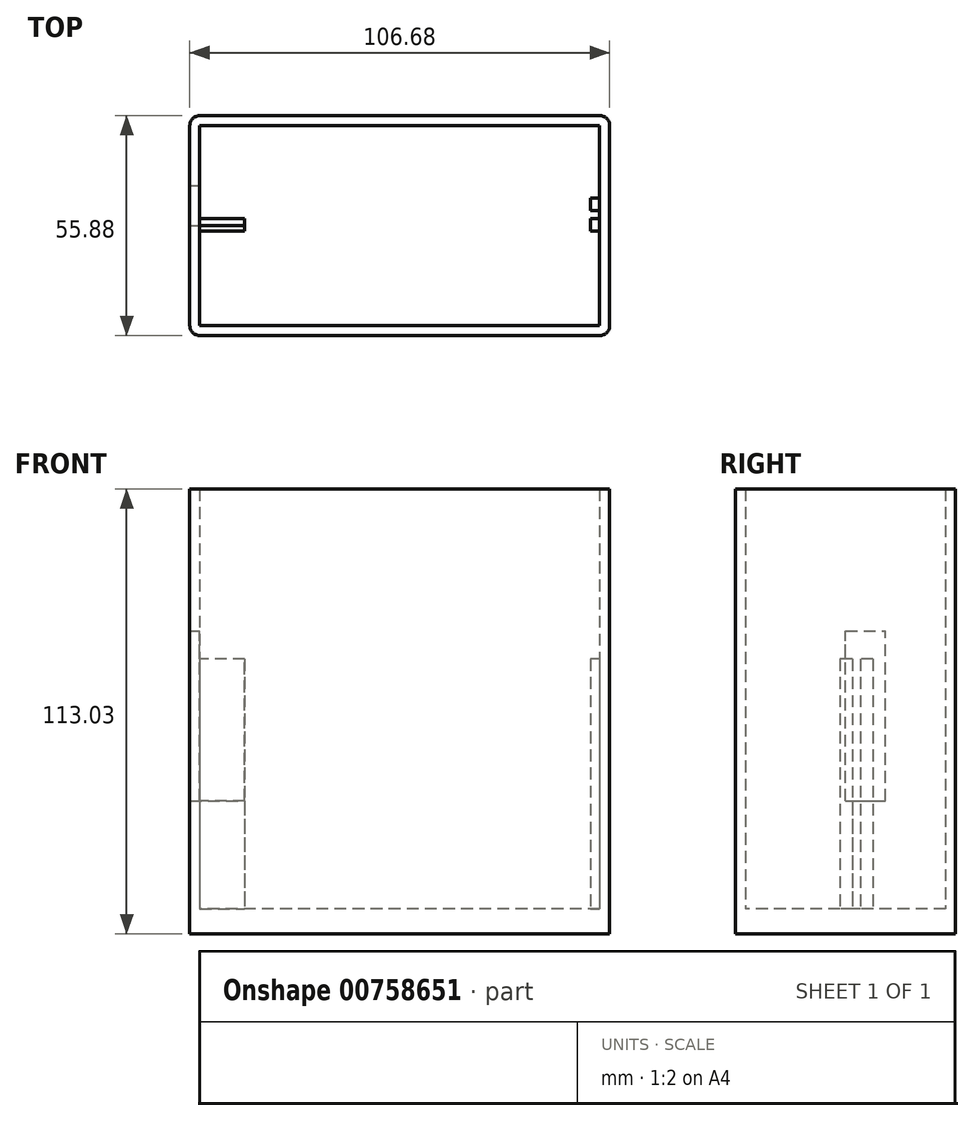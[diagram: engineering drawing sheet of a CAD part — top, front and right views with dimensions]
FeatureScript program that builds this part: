
annotation { "Feature Type Name" : "Feature", "Feature Type Description" : "" }
export const myFeature = defineFeature(function(context is Context, id is Id, definition is map)
    precondition{}
    {
        {
            var Q0;
            Q0=qCreatedBy(makeId("Top.planeOp"),FACE);
            var sketch = newSketch(context, id + "F0", { "sketchPlane" : qUnion([Q0])});
            skLineSegment(sketch, "E0.bottom", {"start": v(50.8, 25.4) * mm, "end": v(-50.8, 25.4) * mm});
            skLineSegment(sketch, "E0.top", {"start": v(50.8, -25.4) * mm, "end": v(-50.8, -25.4) * mm});
            skLineSegment(sketch, "E0.left", {"start": v(50.8, 25.4) * mm, "end": v(50.8, -25.4) * mm});
            skLineSegment(sketch, "E0.right", {"start": v(-50.8, 25.4) * mm, "end": v(-50.8, -25.4) * mm});
            skPoint(sketch, "E0.middle", {"position": v(0, 0) * mm});
            skLineSegment(sketch, "E1.bottom", {"start": v(50.8, 27.94) * mm, "end": v(-50.8, 27.94) * mm});
            skLineSegment(sketch, "E1.top", {"start": v(50.8, -27.94) * mm, "end": v(-50.8, -27.94) * mm});
            skLineSegment(sketch, "E1.left", {"start": v(53.34, 25.4) * mm, "end": v(53.34, -25.4) * mm});
            skLineSegment(sketch, "E1.right", {"start": v(-53.34, 25.4) * mm, "end": v(-53.34, -25.4) * mm});
            skPoint(sketch, "E2.visualSharp", {"position": v(53.34, 27.94) * mm});
            skArc(sketch, "E2.filletArc", {"start": v(53.34, 25.4) * mm, "mid": v(52.6, 27.2) * mm, "end": v(50.8, 27.94) * mm});
            skPoint(sketch, "E3.visualSharp", {"position": v(-53.34, 27.94) * mm});
            skArc(sketch, "E3.filletArc", {"start": v(-50.8, 27.94) * mm, "mid": v(-52.6, 27.2) * mm, "end": v(-53.34, 25.4) * mm});
            skPoint(sketch, "E4.visualSharp", {"position": v(-53.34, -27.94) * mm});
            skArc(sketch, "E4.filletArc", {"start": v(-53.34, -25.4) * mm, "mid": v(-52.6, -27.2) * mm, "end": v(-50.8, -27.94) * mm});
            skPoint(sketch, "E5.visualSharp", {"position": v(53.34, -27.94) * mm});
            skArc(sketch, "E5.filletArc", {"start": v(50.8, -27.94) * mm, "mid": v(52.6, -27.2) * mm, "end": v(53.34, -25.4) * mm});
            skSolve(sketch);
        }
        {
            var Q0;
            Q0=makeQuery(id+"F0.imprint","IMPRINT",FACE,{"disambiguationData":[TD([[makeQuery(id+"F0.imprint","IMPRINT",EDGE,{"derivedFrom":sQuery(id+"F0.wireOp",EDGE,"E0.bottom")}),-1.0]])]});
            extrude(context, id + "F1", {"entities" : qUnion([Q0]), "depth" : 113.03 * mm, "offsetDistance" : 25.4 * mm});
        }
        {
            var Q0;
            Q0=qSketchRegion(id+"F0",true);
            var Q1;
            Q1=makeQuery(id+"F0.imprint","IMPRINT",FACE,{"disambiguationData":[TD([[makeQuery(id+"F0.imprint","IMPRINT",EDGE,{"derivedFrom":sQuery(id+"F0.wireOp",EDGE,"E0.bottom")}),1.0]])]});
            extrude(context, id + "F2", {"entities" : qUnion([Q0, Q1]), "operationType" : NewBodyOperationType.ADD, "depth" : 6.35 * mm, "offsetDistance" : 25.4 * mm});
        }
        {
            var Q0;
            Q0=makeQuery(id+"F2.opExtrude","CAP_FACE",FACE,{"disambiguationData":[OSD([sQuery(id+"F0.wireOp",EDGE,"E1.bottom"),sQuery(id+"F0.wireOp",EDGE,"E1.top"),sQuery(id+"F0.wireOp",EDGE,"E1.left"),sQuery(id+"F0.wireOp",EDGE,"E1.right"),sQuery(id+"F0.wireOp",EDGE,"BYKlQcYZ-631A-2yId-C92L-wMy8uTNsIFIs.bottom"),sQuery(id+"F0.wireOp",EDGE,"BYKlQcYZ-631A-2yId-C92L-wMy8uTNsIFIs.top"),sQuery(id+"F0.wireOp",EDGE,"BYKlQcYZ-631A-2yId-C92L-wMy8uTNsIFIs.left"),sQuery(id+"F0.wireOp",EDGE,"BYKlQcYZ-631A-2yId-C92L-wMy8uTNsIFIs.right"),sQuery(id+"F0.wireOp",EDGE,"E2.filletArc"),sQuery(id+"F0.wireOp",EDGE,"E3.filletArc"),sQuery(id+"F0.wireOp",EDGE,"E4.filletArc"),sQuery(id+"F0.wireOp",EDGE,"E5.filletArc")])],"isStart":false});
            var sketch = newSketch(context, id + "F3", { "sketchPlane" : qUnion([Q0])});
            skLineSegment(sketch, "E6", {"start": v(-50.8, 1.78) * mm, "end": v(-39.37, 1.78) * mm});
            skLineSegment(sketch, "E7", {"start": v(-39.37, 1.78) * mm, "end": v(-39.37, -1.4) * mm});
            skLineSegment(sketch, "E8", {"start": v(-39.37, -1.4) * mm, "end": v(-50.8, -1.4) * mm});
            skSolve(sketch);
        }
        {
            var Q0;
            Q0=qSketchRegion(id+"F3",true);
            var Q1;
            {var subQ0=sQuery(id+"F3.wireOp",EDGE,"lTtmv5Bm-ZFXb-4e8F-iXT5-zUQ0Jz6aJe3K");Q1=makeQuery(id+"F3.imprint","IMPRINT",FACE,{"disambiguationData":[TD([[makeQuery(id+"F3.imprint","IMPRINT",EDGE,{"derivedFrom":subQ0}),-1.0]])]});}
            var Q2;
            {var subQ0=sQuery(id+"F3.wireOp",EDGE,"E6");Q2=makeQuery(id+"F3.imprint","IMPRINT",FACE,{"disambiguationData":[TD([[makeQuery(id+"F3.imprint","IMPRINT",EDGE,{"derivedFrom":subQ0}),-1.0]])]});}
            extrude(context, id + "F4", {"entities" : qUnion([Q0, Q1, Q2]), "operationType" : NewBodyOperationType.ADD, "depth" : 63.5 * mm, "offsetDistance" : 25.4 * mm});
        }
        {
            var Q0;
            Q0=makeQuery(id+"F2.opExtrude","CAP_FACE",FACE,{"disambiguationData":[OSD([sQuery(id+"F0.wireOp",EDGE,"E1.bottom"),sQuery(id+"F0.wireOp",EDGE,"E1.top"),sQuery(id+"F0.wireOp",EDGE,"E1.left"),sQuery(id+"F0.wireOp",EDGE,"E1.right"),sQuery(id+"F0.wireOp",EDGE,"BYKlQcYZ-631A-2yId-C92L-wMy8uTNsIFIs.bottom"),sQuery(id+"F0.wireOp",EDGE,"BYKlQcYZ-631A-2yId-C92L-wMy8uTNsIFIs.top"),sQuery(id+"F0.wireOp",EDGE,"BYKlQcYZ-631A-2yId-C92L-wMy8uTNsIFIs.left"),sQuery(id+"F0.wireOp",EDGE,"BYKlQcYZ-631A-2yId-C92L-wMy8uTNsIFIs.right"),sQuery(id+"F0.wireOp",EDGE,"E2.filletArc"),sQuery(id+"F0.wireOp",EDGE,"E3.filletArc"),sQuery(id+"F0.wireOp",EDGE,"E4.filletArc"),sQuery(id+"F0.wireOp",EDGE,"E5.filletArc")])],"isStart":false});
            var sketch = newSketch(context, id + "F5", { "sketchPlane" : qUnion([Q0])});
            skLineSegment(sketch, "E9", {"start": v(50.8, 6.99) * mm, "end": v(48.51, 6.99) * mm});
            skLineSegment(sketch, "E10", {"start": v(48.51, 6.99) * mm, "end": v(48.51, 3.81) * mm});
            skLineSegment(sketch, "E11", {"start": v(48.51, 3.81) * mm, "end": v(50.8, 3.81) * mm});
            skLineSegment(sketch, "E12", {"start": v(50.8, 1.78) * mm, "end": v(48.51, 1.78) * mm});
            skLineSegment(sketch, "E13", {"start": v(48.51, 1.78) * mm, "end": v(48.51, -1.4) * mm});
            skLineSegment(sketch, "E14", {"start": v(48.51, -1.4) * mm, "end": v(50.8, -1.4) * mm});
            skSolve(sketch);
        }
        {
            var Q0;
            Q0=qSketchRegion(id+"F5",true);
            var Q1;
            {var subQ0=sQuery(id+"F5.wireOp",EDGE,"E9");Q1=makeQuery(id+"F5.imprint","IMPRINT",FACE,{"disambiguationData":[TD([[makeQuery(id+"F5.imprint","IMPRINT",EDGE,{"derivedFrom":subQ0}),1.0]])]});}
            var Q2;
            {var subQ0=sQuery(id+"F5.wireOp",EDGE,"E12");Q2=makeQuery(id+"F5.imprint","IMPRINT",FACE,{"disambiguationData":[TD([[makeQuery(id+"F5.imprint","IMPRINT",EDGE,{"derivedFrom":subQ0}),1.0]])]});}
            extrude(context, id + "F6", {"entities" : qUnion([Q0, Q1, Q2]), "operationType" : NewBodyOperationType.ADD, "depth" : 63.5 * mm, "offsetDistance" : 25.4 * mm});
        }
        {
            var Q0;
            Q0=qCreatedBy(makeId("Right.planeOp"),FACE);
            var sketch = newSketch(context, id + "F7", { "sketchPlane" : qUnion([Q0])});
            skLineSegment(sketch, "E15.bottom", {"start": v(0, 33.78) * mm, "end": v(10.16, 33.78) * mm});
            skLineSegment(sketch, "E15.top", {"start": v(0, 76.96) * mm, "end": v(10.16, 76.96) * mm});
            skLineSegment(sketch, "E15.left", {"start": v(0, 33.78) * mm, "end": v(0, 76.96) * mm});
            skLineSegment(sketch, "E15.right", {"start": v(10.16, 33.78) * mm, "end": v(10.16, 76.96) * mm});
            skSolve(sketch);
        }
        {
            var Q0;
            Q0 = qSketchRegion(id + "F7", true);
            extrude(context, id + "F8", {"entities" : qUnion([Q0]), "operationType" : NewBodyOperationType.REMOVE, "oppositeDirection" : true, "depth" : 73.66 * mm, "offsetDistance" : 25.4 * mm});
        }
    });
